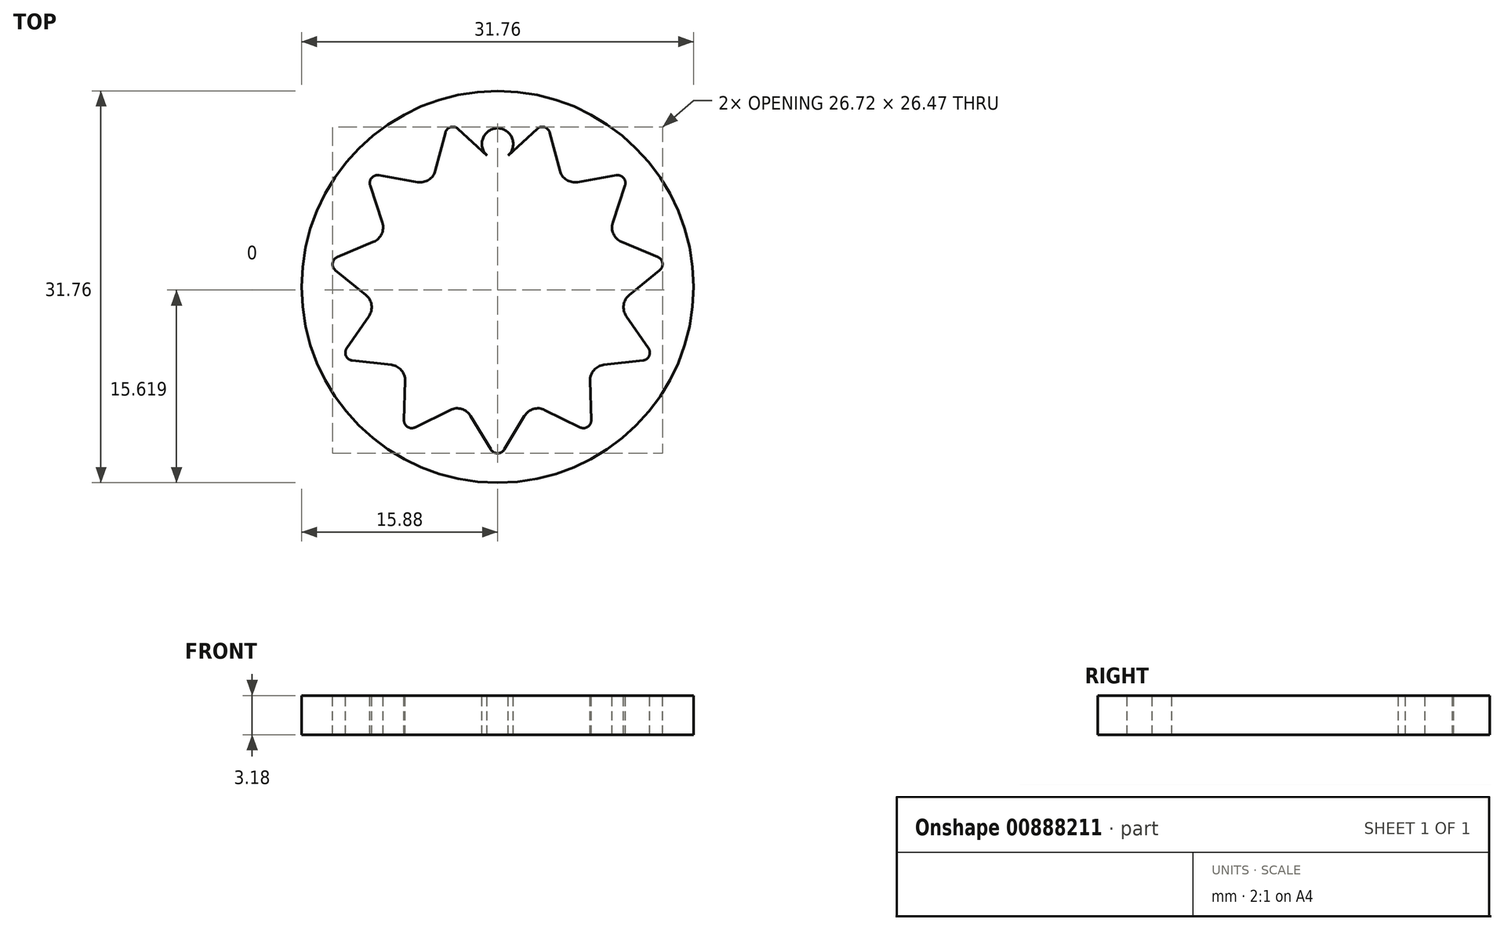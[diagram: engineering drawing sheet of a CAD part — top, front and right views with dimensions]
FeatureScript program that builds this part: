
annotation { "Feature Type Name" : "Feature", "Feature Type Description" : "" }
export const myFeature = defineFeature(function(context is Context, id is Id, definition is map)
    precondition{}
    {
        {
            var Q0;
            Q0=qCreatedBy(makeId("Top.planeOp"),FACE);
            var sketch = newSketch(context, id + "F0", { "sketchPlane" : qUnion([Q0])});
            skCircle(sketch, "E0", {"center": v(0, 0) * mm, "radius": 13.5 * mm});
            skLineSegment(sketch, "E1", {"start": v(0, 13.5) * mm, "end": v(0, 10.32) * mm});
            skCircle(sketch, "E2", {"center": v(0, 11.59) * mm, "radius": 1.27 * mm});
            skCircle(sketch, "E3.1.0", {"center": v(-6.27, 9.75) * mm, "radius": 1.27 * mm});
            skCircle(sketch, "E3.2.0", {"center": v(-10.54, 4.81) * mm, "radius": 1.27 * mm});
            skCircle(sketch, "E3.3.0", {"center": v(-11.47, -1.65) * mm, "radius": 1.27 * mm});
            skCircle(sketch, "E3.4.0", {"center": v(-8.76, -7.59) * mm, "radius": 1.27 * mm});
            skCircle(sketch, "E3.5.0", {"center": v(-3.26, -11.12) * mm, "radius": 1.27 * mm});
            skCircle(sketch, "E3.6.0", {"center": v(3.26, -11.12) * mm, "radius": 1.27 * mm});
            skCircle(sketch, "E3.7.0", {"center": v(8.76, -7.59) * mm, "radius": 1.27 * mm});
            skCircle(sketch, "E3.8.0", {"center": v(11.47, -1.65) * mm, "radius": 1.27 * mm});
            skCircle(sketch, "E3.9.0", {"center": v(10.54, 4.81) * mm, "radius": 1.27 * mm});
            skCircle(sketch, "E3.10.0", {"center": v(6.27, 9.75) * mm, "radius": 1.27 * mm});
            skLineSegment(sketch, "E4", {"start": v(0, 0) * mm, "end": v(3.8, 12.95) * mm});
            skCircle(sketch, "E5", {"center": v(3.62, 12.34) * mm, "radius": 0.64 * mm});
            skCircle(sketch, "E6.1.0", {"center": v(-3.62, 12.34) * mm, "radius": 0.64 * mm});
            skCircle(sketch, "E6.2.0", {"center": v(-9.72, 8.42) * mm, "radius": 0.64 * mm});
            skCircle(sketch, "E7.1.3.0", {"center": v(-12.73, 1.83) * mm, "radius": 0.64 * mm});
            skCircle(sketch, "E7.1.4.0", {"center": v(-11.7, -5.34) * mm, "radius": 0.64 * mm});
            skCircle(sketch, "E7.1.5.0", {"center": v(-6.95, -10.82) * mm, "radius": 0.64 * mm});
            skCircle(sketch, "E7.1.6.0", {"center": v(0, -12.86) * mm, "radius": 0.64 * mm});
            skCircle(sketch, "E7.1.7.0", {"center": v(6.95, -10.82) * mm, "radius": 0.64 * mm});
            skCircle(sketch, "E7.1.8.0", {"center": v(11.7, -5.34) * mm, "radius": 0.64 * mm});
            skCircle(sketch, "E7.1.9.0", {"center": v(12.73, 1.83) * mm, "radius": 0.64 * mm});
            skCircle(sketch, "E7.1.10.0", {"center": v(9.72, 8.42) * mm, "radius": 0.64 * mm});
            skLineSegment(sketch, "E8", {"start": v(-9.33, 5.2) * mm, "end": v(-10.32, 8.22) * mm});
            skLineSegment(sketch, "E9", {"start": v(-10.05, 3.64) * mm, "end": v(-12.97, 2.42) * mm});
            skLineSegment(sketch, "E10", {"start": v(-9.6, 9.05) * mm, "end": v(-6.48, 8.5) * mm});
            skLineSegment(sketch, "E11", {"start": v(-13.13, 1.34) * mm, "end": v(-10.67, -0.66) * mm});
            skLineSegment(sketch, "E12", {"start": v(-10.42, -2.37) * mm, "end": v(-12.22, -4.98) * mm});
            skLineSegment(sketch, "E13", {"start": v(-7.49, -7.63) * mm, "end": v(-7.59, -10.8) * mm});
            skLineSegment(sketch, "E14", {"start": v(-6.67, -11.39) * mm, "end": v(-3.83, -9.98) * mm});
            skLineSegment(sketch, "E15", {"start": v(-2.18, -10.47) * mm, "end": v(-0.54, -13.19) * mm});
            skLineSegment(sketch, "E16", {"start": v(0.54, -13.19) * mm, "end": v(2.18, -10.47) * mm});
            skLineSegment(sketch, "E17", {"start": v(3.83, -9.98) * mm, "end": v(6.67, -11.39) * mm});
            skLineSegment(sketch, "E18", {"start": v(7.59, -10.8) * mm, "end": v(7.49, -7.63) * mm});
            skLineSegment(sketch, "E19", {"start": v(8.62, -6.33) * mm, "end": v(11.77, -5.97) * mm});
            skLineSegment(sketch, "E20", {"start": v(-5.04, 9.43) * mm, "end": v(-4.24, 12.5) * mm});
            skLineSegment(sketch, "E21", {"start": v(-3.2, 12.8) * mm, "end": v(-0.86, 10.66) * mm});
            skLineSegment(sketch, "E22", {"start": v(0.86, 10.66) * mm, "end": v(3.2, 12.8) * mm});
            skLineSegment(sketch, "E23", {"start": v(10.32, 8.22) * mm, "end": v(9.33, 5.2) * mm});
            skLineSegment(sketch, "E24", {"start": v(10.05, 3.64) * mm, "end": v(12.97, 2.42) * mm});
            skLineSegment(sketch, "E25", {"start": v(13.13, 1.34) * mm, "end": v(10.67, -0.66) * mm});
            skLineSegment(sketch, "E26", {"start": v(10.42, -2.37) * mm, "end": v(12.22, -4.98) * mm});
            skLineSegment(sketch, "E27", {"start": v(4.24, 12.5) * mm, "end": v(5.04, 9.43) * mm});
            skLineSegment(sketch, "E28", {"start": v(6.48, 8.5) * mm, "end": v(9.6, 9.05) * mm});
            skLineSegment(sketch, "E29", {"start": v(-11.77, -5.97) * mm, "end": v(-8.62, -6.33) * mm});
            skCircle(sketch, "E30", {"center": v(0, 0) * mm, "radius": 15.88 * mm});
            skSolve(sketch);
        }
        {
            var Q0;
            Q0=makeQuery(id+"F0.imprint","IMPRINT",FACE,{"disambiguationData":[TD([[makeQuery(id+"F0.imprint","IMPRINT",EDGE,{"derivedFrom":sQuery(id+"F0.wireOp",EDGE,"E30")}),1.0]])]});
            var Q1;
            {var subQ0=sQuery(id+"F0.wireOp",EDGE,"E10");Q1=makeQuery(id+"F0.imprint","IMPRINT",FACE,{"disambiguationData":[TD([[makeQuery(id+"F0.imprint","IMPRINT",EDGE,{"derivedFrom":subQ0}),1.0]])]});}
            var Q2;
            {var subQ0=sQuery(id+"F0.wireOp",EDGE,"E3.1.0");var subQ1=makeQuery(id+"F0.imprint","INTERSECT",VERTEX,{"derivedFrom":[subQ0,sQuery(id+"F0.wireOp",EDGE,"E10")]});Q2=makeQuery(id+"F0.imprint","IMPRINT",FACE,{"disambiguationData":[TD([[makeQuery(id+"F0.imprint","IMPRINT",EDGE,{"disambiguationData":[TD([[subQ1,-1.0]])],"derivedFrom":subQ0}),1.0]])]});}
            var Q3;
            {var subQ4=sQuery(id+"F0.wireOp",EDGE,"E11");Q3=makeQuery(id+"F0.imprint","IMPRINT",FACE,{"disambiguationData":[TD([[makeQuery(id+"F0.imprint","IMPRINT",EDGE,{"derivedFrom":subQ4}),-1.0]])]});}
            var Q4;
            {var subQ0=sQuery(id+"F0.wireOp",EDGE,"E3.3.0");var subQ1=makeQuery(id+"F0.imprint","INTERSECT",VERTEX,{"derivedFrom":[subQ0,sQuery(id+"F0.wireOp",EDGE,"E11")]});Q4=makeQuery(id+"F0.imprint","IMPRINT",FACE,{"disambiguationData":[TD([[makeQuery(id+"F0.imprint","IMPRINT",EDGE,{"disambiguationData":[TD([[subQ1,1.0]])],"derivedFrom":subQ0}),1.0]])]});}
            var Q5;
            {var subQ6=sQuery(id+"F0.wireOp",EDGE,"E8");Q5=makeQuery(id+"F0.imprint","IMPRINT",FACE,{"disambiguationData":[TD([[makeQuery(id+"F0.imprint","IMPRINT",EDGE,{"derivedFrom":subQ6}),1.0]])]});}
            var Q6;
            {var subQ0=sQuery(id+"F0.wireOp",EDGE,"E3.2.0");var subQ1=makeQuery(id+"F0.imprint","INTERSECT",VERTEX,{"derivedFrom":[subQ0,sQuery(id+"F0.wireOp",EDGE,"E8")]});Q6=makeQuery(id+"F0.imprint","IMPRINT",FACE,{"disambiguationData":[TD([[makeQuery(id+"F0.imprint","IMPRINT",EDGE,{"disambiguationData":[TD([[subQ1,1.0]])],"derivedFrom":subQ0}),1.0]])]});}
            var Q7;
            {var subQ0=sQuery(id+"F0.wireOp",EDGE,"E21");Q7=makeQuery(id+"F0.imprint","IMPRINT",FACE,{"disambiguationData":[TD([[makeQuery(id+"F0.imprint","IMPRINT",EDGE,{"derivedFrom":subQ0}),1.0]])]});}
            var Q8;
            {var subQ0=sQuery(id+"F0.wireOp",EDGE,"E2");var subQ1=sQuery(id+"F0.wireOp",EDGE,"E1");var subQ2=makeQuery(id+"F0.imprint","INTERSECT",VERTEX,{"disambiguationData":[OD(0.0)],"derivedFrom":[subQ1,subQ0]});Q8=makeQuery(id+"F0.imprint","IMPRINT",FACE,{"disambiguationData":[TD([[makeQuery(id+"F0.imprint","IMPRINT",EDGE,{"disambiguationData":[TD([[subQ2,1.0]])],"derivedFrom":subQ1}),1.0]])]});}
            var Q9;
            {var subQ3=sQuery(id+"F0.wireOp",EDGE,"E22");Q9=makeQuery(id+"F0.imprint","IMPRINT",FACE,{"disambiguationData":[TD([[makeQuery(id+"F0.imprint","IMPRINT",EDGE,{"derivedFrom":subQ3}),1.0]])]});}
            var Q10;
            {var subQ0=sQuery(id+"F0.wireOp",EDGE,"E2");var subQ1=sQuery(id+"F0.wireOp",EDGE,"E1");var subQ2=makeQuery(id+"F0.imprint","INTERSECT",VERTEX,{"disambiguationData":[OD(0.0)],"derivedFrom":[subQ1,subQ0]});Q10=makeQuery(id+"F0.imprint","IMPRINT",FACE,{"disambiguationData":[TD([[makeQuery(id+"F0.imprint","IMPRINT",EDGE,{"disambiguationData":[TD([[subQ2,1.0]])],"derivedFrom":subQ1}),-1.0]])]});}
            var Q11;
            {var subQ3=sQuery(id+"F0.wireOp",EDGE,"E27");Q11=makeQuery(id+"F0.imprint","IMPRINT",FACE,{"disambiguationData":[TD([[makeQuery(id+"F0.imprint","IMPRINT",EDGE,{"derivedFrom":subQ3}),1.0]])]});}
            var Q12;
            {var subQ0=sQuery(id+"F0.wireOp",EDGE,"E3.10.0");var subQ1=makeQuery(id+"F0.imprint","INTERSECT",VERTEX,{"derivedFrom":[subQ0,sQuery(id+"F0.wireOp",EDGE,"E27")]});Q12=makeQuery(id+"F0.imprint","IMPRINT",FACE,{"disambiguationData":[TD([[makeQuery(id+"F0.imprint","IMPRINT",EDGE,{"disambiguationData":[TD([[subQ1,-1.0]])],"derivedFrom":subQ0}),1.0]])]});}
            var Q13;
            {var subQ4=sQuery(id+"F0.wireOp",EDGE,"E23");Q13=makeQuery(id+"F0.imprint","IMPRINT",FACE,{"disambiguationData":[TD([[makeQuery(id+"F0.imprint","IMPRINT",EDGE,{"derivedFrom":subQ4}),1.0]])]});}
            var Q14;
            {var subQ0=sQuery(id+"F0.wireOp",EDGE,"E3.9.0");var subQ1=makeQuery(id+"F0.imprint","INTERSECT",VERTEX,{"derivedFrom":[subQ0,sQuery(id+"F0.wireOp",EDGE,"E23")]});Q14=makeQuery(id+"F0.imprint","IMPRINT",FACE,{"disambiguationData":[TD([[makeQuery(id+"F0.imprint","IMPRINT",EDGE,{"disambiguationData":[TD([[subQ1,-1.0]])],"derivedFrom":subQ0}),1.0]])]});}
            var Q15;
            {var subQ0=sQuery(id+"F0.wireOp",EDGE,"E25");Q15=makeQuery(id+"F0.imprint","IMPRINT",FACE,{"disambiguationData":[TD([[makeQuery(id+"F0.imprint","IMPRINT",EDGE,{"derivedFrom":subQ0}),1.0]])]});}
            var Q16;
            {var subQ0=sQuery(id+"F0.wireOp",EDGE,"E3.8.0");var subQ1=makeQuery(id+"F0.imprint","INTERSECT",VERTEX,{"derivedFrom":[subQ0,sQuery(id+"F0.wireOp",EDGE,"E25")]});Q16=makeQuery(id+"F0.imprint","IMPRINT",FACE,{"disambiguationData":[TD([[makeQuery(id+"F0.imprint","IMPRINT",EDGE,{"disambiguationData":[TD([[subQ1,-1.0]])],"derivedFrom":subQ0}),1.0]])]});}
            var Q17;
            {var subQ4=sQuery(id+"F0.wireOp",EDGE,"E18");Q17=makeQuery(id+"F0.imprint","IMPRINT",FACE,{"disambiguationData":[TD([[makeQuery(id+"F0.imprint","IMPRINT",EDGE,{"derivedFrom":subQ4}),-1.0]])]});}
            var Q18;
            {var subQ0=sQuery(id+"F0.wireOp",EDGE,"E3.7.0");var subQ1=makeQuery(id+"F0.imprint","INTERSECT",VERTEX,{"derivedFrom":[subQ0,sQuery(id+"F0.wireOp",EDGE,"E18")]});Q18=makeQuery(id+"F0.imprint","IMPRINT",FACE,{"disambiguationData":[TD([[makeQuery(id+"F0.imprint","IMPRINT",EDGE,{"disambiguationData":[TD([[subQ1,1.0]])],"derivedFrom":subQ0}),1.0]])]});}
            var Q19;
            {var subQ4=sQuery(id+"F0.wireOp",EDGE,"E16");Q19=makeQuery(id+"F0.imprint","IMPRINT",FACE,{"disambiguationData":[TD([[makeQuery(id+"F0.imprint","IMPRINT",EDGE,{"derivedFrom":subQ4}),-1.0]])]});}
            var Q20;
            {var subQ0=sQuery(id+"F0.wireOp",EDGE,"E3.6.0");var subQ1=makeQuery(id+"F0.imprint","INTERSECT",VERTEX,{"derivedFrom":[subQ0,sQuery(id+"F0.wireOp",EDGE,"E16")]});Q20=makeQuery(id+"F0.imprint","IMPRINT",FACE,{"disambiguationData":[TD([[makeQuery(id+"F0.imprint","IMPRINT",EDGE,{"disambiguationData":[TD([[subQ1,1.0]])],"derivedFrom":subQ0}),1.0]])]});}
            var Q21;
            {var subQ0=sQuery(id+"F0.wireOp",EDGE,"E14");Q21=makeQuery(id+"F0.imprint","IMPRINT",FACE,{"disambiguationData":[TD([[makeQuery(id+"F0.imprint","IMPRINT",EDGE,{"derivedFrom":subQ0}),-1.0]])]});}
            var Q22;
            {var subQ0=sQuery(id+"F0.wireOp",EDGE,"E3.5.0");var subQ1=makeQuery(id+"F0.imprint","INTERSECT",VERTEX,{"derivedFrom":[subQ0,sQuery(id+"F0.wireOp",EDGE,"E14")]});Q22=makeQuery(id+"F0.imprint","IMPRINT",FACE,{"disambiguationData":[TD([[makeQuery(id+"F0.imprint","IMPRINT",EDGE,{"disambiguationData":[TD([[subQ1,1.0]])],"derivedFrom":subQ0}),1.0]])]});}
            var Q23;
            {var subQ4=sQuery(id+"F0.wireOp",EDGE,"E13");Q23=makeQuery(id+"F0.imprint","IMPRINT",FACE,{"disambiguationData":[TD([[makeQuery(id+"F0.imprint","IMPRINT",EDGE,{"derivedFrom":subQ4}),-1.0]])]});}
            var Q24;
            {var subQ0=sQuery(id+"F0.wireOp",EDGE,"E3.4.0");var subQ1=makeQuery(id+"F0.imprint","INTERSECT",VERTEX,{"derivedFrom":[subQ0,sQuery(id+"F0.wireOp",EDGE,"E13")]});Q24=makeQuery(id+"F0.imprint","IMPRINT",FACE,{"disambiguationData":[TD([[makeQuery(id+"F0.imprint","IMPRINT",EDGE,{"disambiguationData":[TD([[subQ1,-1.0]])],"derivedFrom":subQ0}),1.0]])]});}
            extrude(context, id + "F1", {"entities" : qUnion([Q0, Q1, Q2, Q3, Q4, Q5, Q6, Q7, Q8, Q9, Q10, Q11, Q12, Q13, Q14, Q15, Q16, Q17, Q18, Q19, Q20, Q21, Q22, Q23, Q24]), "oppositeDirection" : true, "depth" : 3.17 * mm, "offsetDistance" : 25.4 * mm});
        }
    });
